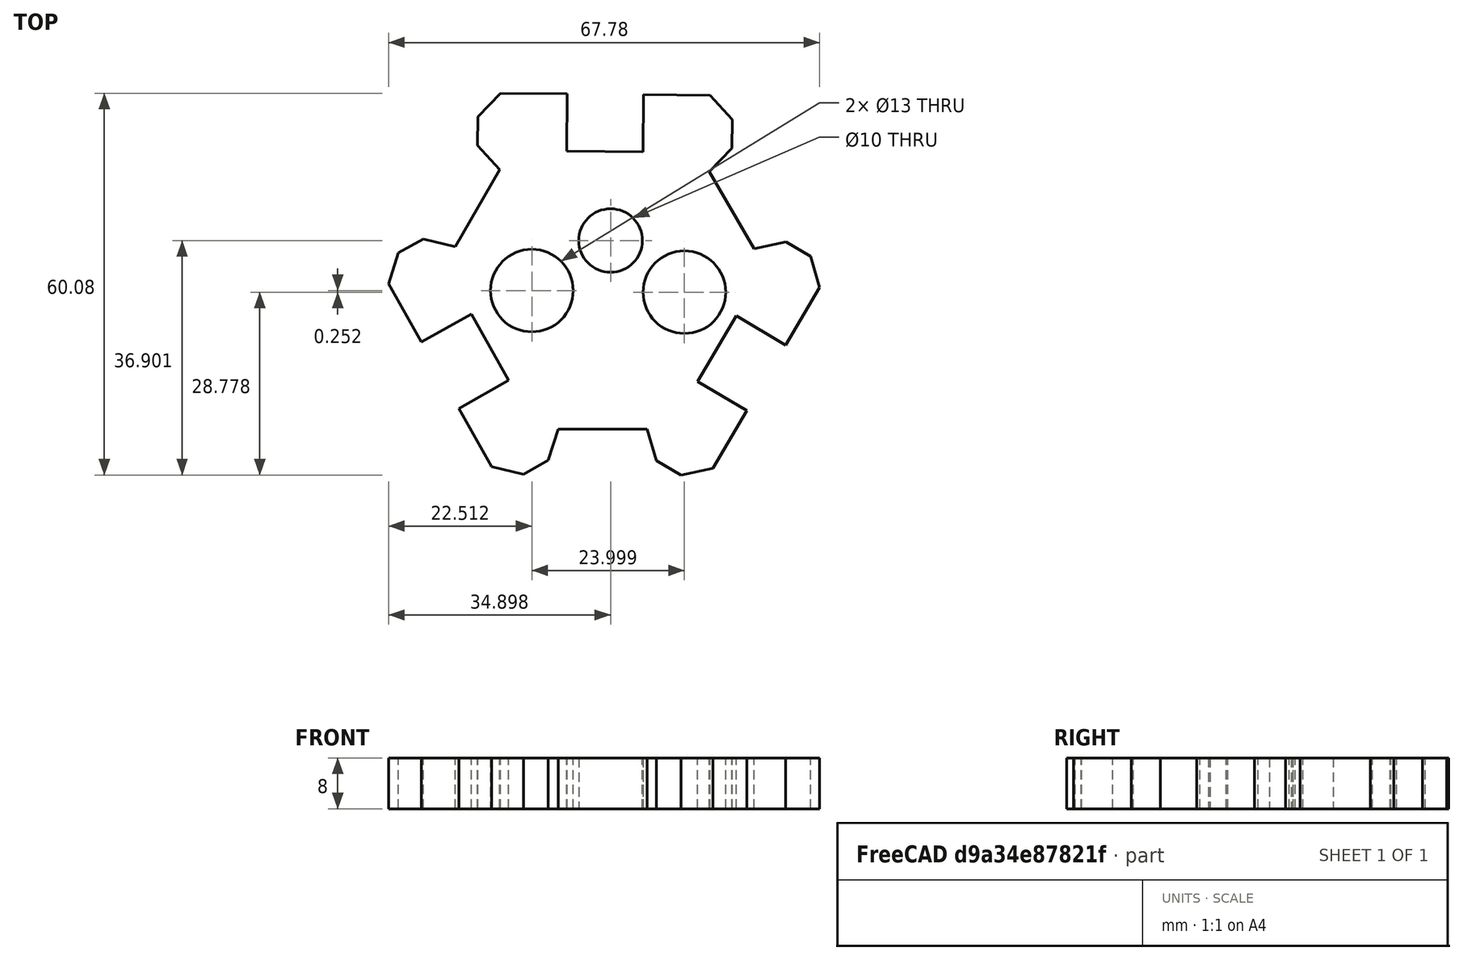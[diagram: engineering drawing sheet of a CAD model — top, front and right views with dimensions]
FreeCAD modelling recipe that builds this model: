
FCSTD DOCUMENT  (FreeCAD 0.17R13522 (Git))
Label: baseExtruder
License: All rights reserved
LicenseURL: http://en.wikipedia.org/wiki/All_rights_reserved
objects: Sketcher::SketchObject×1, Part::Extrusion×1
note: 2 computed .brp shape members not serialized (recipe doc carries the construction recipe); baked Part::Feature solids carry a one-line shape summary decoded from their .brp

FEATURE [Sketcher::SketchObject] Sketch
  sketch-geometry (39):
    g0: LineSegment StartX=92.1382 StartY=71.478 StartZ=0 EndX=99.1382 EndY=59.3536 EndZ=0
    g1: LineSegment StartX=68.3387 StartY=30.9498 StartZ=0 EndX=82.3387 EndY=30.9498 EndZ=0
    g2: LineSegment StartX=59.14 StartY=71.8249 StartZ=0 EndX=52.14 EndY=59.7005 EndZ=0
    g3: LineSegment StartX=82.3387 StartY=30.9498 StartZ=0 EndX=83.7847 EndY=26.0283 EndZ=0
    g4: LineSegment StartX=83.7847 StartY=26.0283 StartZ=0 EndX=87.6579 EndY=23.7374 EndZ=0
    g5: LineSegment StartX=87.6579 StartY=23.7374 StartZ=0 EndX=92.6674 EndY=24.8409 EndZ=0
    g6: LineSegment StartX=92.6674 StartY=24.8409 StartZ=0 EndX=98.0127 EndY=33.8785 EndZ=0
    g7: LineSegment StartX=98.0127 StartY=33.8785 StartZ=0 EndX=90.2662 EndY=38.4602 EndZ=0
    g8: LineSegment StartX=90.2662 StartY=38.4602 StartZ=0 EndX=96.3751 EndY=48.7888 EndZ=0
    g9: LineSegment StartX=96.3751 StartY=48.7888 StartZ=0 EndX=104.122 EndY=44.2072 EndZ=0
    g10: LineSegment StartX=104.122 StartY=44.2072 StartZ=0 EndX=109.467 EndY=53.2447 EndZ=0
    g11: LineSegment StartX=109.467 StartY=53.2447 StartZ=0 EndX=108.021 EndY=58.1663 EndZ=0
    g12: LineSegment StartX=108.021 StartY=58.1663 StartZ=0 EndX=104.148 EndY=60.4571 EndZ=0
    g13: LineSegment StartX=104.148 StartY=60.4571 StartZ=0 EndX=99.1382 EndY=59.3536 EndZ=0
    g14: LineSegment StartX=92.1382 StartY=71.478 StartZ=0 EndX=95.6774 EndY=75.191 EndZ=0
    g15: LineSegment StartX=95.6774 StartY=75.191 StartZ=0 EndX=95.7247 EndY=79.6908 EndZ=0
    g16: LineSegment StartX=95.7247 StartY=79.6908 StartZ=0 EndX=92.2644 EndY=83.4773 EndZ=0
    g17: LineSegment StartX=92.2644 StartY=83.4773 StartZ=0 EndX=81.7649 EndY=83.5877 EndZ=0
    g18: LineSegment StartX=81.7649 StartY=83.5877 StartZ=0 EndX=81.6703 EndY=74.5882 EndZ=0
    g19: LineSegment StartX=81.6703 StartY=74.5882 StartZ=0 EndX=69.671 EndY=74.7143 EndZ=0
    g20: LineSegment StartX=69.671 StartY=74.7143 StartZ=0 EndX=69.7656 EndY=83.7138 EndZ=0
    g21: LineSegment StartX=69.7656 StartY=83.7138 StartZ=0 EndX=59.2662 EndY=83.8242 EndZ=0
    g22: LineSegment StartX=59.2662 StartY=83.8242 StartZ=0 EndX=55.727 EndY=80.1112 EndZ=0
    g23: LineSegment StartX=55.727 StartY=80.1112 StartZ=0 EndX=55.6796 EndY=75.6115 EndZ=0
    g24: LineSegment StartX=55.6796 StartY=75.6115 StartZ=0 EndX=59.14 EndY=71.8249 EndZ=0
    g25: LineSegment StartX=52.14 StartY=59.7005 StartZ=0 EndX=47.1537 EndY=60.9041 EndZ=0
    g26: LineSegment StartX=47.1537 StartY=60.9041 StartZ=0 EndX=43.2331 EndY=58.6952 EndZ=0
    g27: LineSegment StartX=43.2331 StartY=58.6952 StartZ=0 EndX=41.6889 EndY=53.8036 EndZ=0
    g28: LineSegment StartX=41.6889 StartY=53.8036 StartZ=0 EndX=46.8412 EndY=44.6589 EndZ=0
    g29: LineSegment StartX=46.8412 StartY=44.6589 StartZ=0 EndX=54.6823 EndY=49.0767 EndZ=0
    g30: LineSegment StartX=54.6823 StartY=49.0767 StartZ=0 EndX=60.5727 EndY=38.6219 EndZ=0
    g31: LineSegment StartX=60.5727 StartY=38.6219 StartZ=0 EndX=52.7316 EndY=34.2041 EndZ=0
    g32: LineSegment StartX=52.7316 StartY=34.2041 StartZ=0 EndX=57.8876 EndY=25.0529 EndZ=0
    g33: LineSegment StartX=57.8876 StartY=25.0529 StartZ=0 EndX=62.874 EndY=23.8493 EndZ=0
    g34: LineSegment StartX=62.874 StartY=23.8493 StartZ=0 EndX=66.7945 EndY=26.0582 EndZ=0
    g35: LineSegment StartX=66.7945 StartY=26.0582 StartZ=0 EndX=68.3387 EndY=30.9498 EndZ=0
    g36: Circle CenterX=76.5882 CenterY=60.6409 CenterZ=0 NormalX=0 NormalY=0 NormalZ=1 AngleXU=0 Radius=5
    g37: Circle CenterX=64.202 CenterY=52.7706 CenterZ=0 NormalX=0 NormalY=0 NormalZ=1 AngleXU=0 Radius=6.5
    g38: Circle CenterX=88.2006 CenterY=52.5183 CenterZ=0 NormalX=0 NormalY=0 NormalZ=1 AngleXU=0 Radius=6.5
  constraints (112):
    c: Angle(g0,g1) = 1.0472
    c: Equal(g2,g0)
    c: Equal(g0,g1)
    c: Distance(g2,g2) = 14
    c: Horizontal(g1)
    c: Angle(g1,g2) = 1.0472
    c: Distance(g0,g1) = 33
    c: Distance(g0,g2) = 33
    c: Distance(g2,g1) = 33
    c: Coincident(g1,g3)
    c: Coincident(g3,g4)
    c: Coincident(g4,g5)
    c: Coincident(g5,g6)
    c: Coincident(g6,g7)
    c: Coincident(g7,g8)
    c: Coincident(g8,g9)
    c: Coincident(g9,g10)
    c: Coincident(g10,g11)
    c: Coincident(g11,g12)
    c: Coincident(g12,g13)
    c: Coincident(g13,g0)
    c: Equal(g10,g6)
    c: Perpendicular(g8,g9)
    c: Perpendicular(g7,g8)
    c: Perpendicular(g10,g9)
    c: Perpendicular(g6,g7)
    c: Equal(g7,g9)
    c: Distance(g7,g6) = 9
    c: Distance(g0,g10) = 12
    c: Distance(g1,g5) = 12
    c: Distance(g11,g9) = 14
    c: Distance(g12,g9) = 14
    c: Distance(g5,g10) = 33
    c: Distance(g4,g7) = 14
    c: Distance(g3,g7) = 14
    c: Equal(g4,g12)
    c: Distance(g3,g4) = 4.5
    c: Equal(g4,g12)
    c: Equal(g5,g3)
    c: Equal(g3,g11)
    c: Equal(g11,g13)
    c: Distance(g8,g7) = 12
    c: Coincident(g0,g14)
    c: Coincident(g14,g15)
    c: Coincident(g15,g16)
    c: Coincident(g16,g17)
    c: Coincident(g17,g18)
    c: Coincident(g18,g19)
    c: Coincident(g19,g20)
    c: Coincident(g20,g21)
    c: Coincident(g21,g22)
    c: Coincident(g22,g23)
    c: Coincident(g23,g24)
    c: Coincident(g24,g2)
    c: Distance(g16,g21) = 33
    c: Distance(g19,g18) = 12
    c: Perpendicular(g20,g19)
    c: Perpendicular(g18,g19)
    c: Perpendicular(g18,g17)
    c: Perpendicular(g21,g20)
    c: Equal(g18,g20)
    c: Equal(g21,g17)
    c: Distance(g18,g17) = 9
    c: Distance(g0,g16) = 12
    c: Distance(g2,g21) = 12
    c: Distance(g22,g20) = 14
    c: Distance(g23,g20) = 14
    c: Distance(g15,g18) = 14
    c: Distance(g14,g18) = 14
    c: Equal(g14,g16)
    c: Equal(g16,g22)
    c: Equal(g22,g24)
    c: Equal(g23,g15)
    c: Distance(g23,g22) = 4.5
    c: Coincident(g2,g25)
    c: Coincident(g25,g26)
    c: Coincident(g26,g27)
    c: Coincident(g27,g28)
    c: Coincident(g28,g29)
    c: Coincident(g29,g30)
    c: Coincident(g30,g31)
    c: Coincident(g31,g32)
    c: Coincident(g32,g33)
    c: Coincident(g33,g34)
    c: Coincident(g34,g35)
    c: Coincident(g35,g1)
    c: Distance(g28,g29) = 9
    c: Equal(g29,g31)
    c: Distance(g29,g30) = 12
    c: Perpendicular(g30,g29)
    c: Perpendicular(g31,g30)
    c: Perpendicular(g29,g28)
    c: Perpendicular(g32,g31)
    c: Distance(g27,g32) = 33
    c: Distance(g2,g27) = 12
    c: Distance(g32,g1) = 12
    c: Distance(g26,g29) = 14
    c: Distance(g25,g29) = 14
    c: Distance(g34,g31) = 14
    c: Distance(g33,g31) = 14
    c: Equal(g26,g34)
    c: Distance(g25,g26) = 4.5
    c: Equal(g25,g27)
    c: Equal(g27,g33)
    c: Equal(g33,g35)
    c: Radius(g37) = 6.5
    c: Radius(g38) = 6.5
    c: Radius(g36) = 5
    c: Distance(g36,g19) = 14
    c: Distance(g37,g38) = 24
    c: Distance(g38,g17) = 31
    c: Distance(g37,g21) = 31
FEATURE [Part::Extrusion] Extrude
  Base = -> Sketch
  Dir = (0,0,1)
  DirMode = 2
  FaceMakerClass = Part::FaceMakerBullseye
  LengthFwd = 8
  LengthRev = 0
  Solid = true
  Symmetric = false
